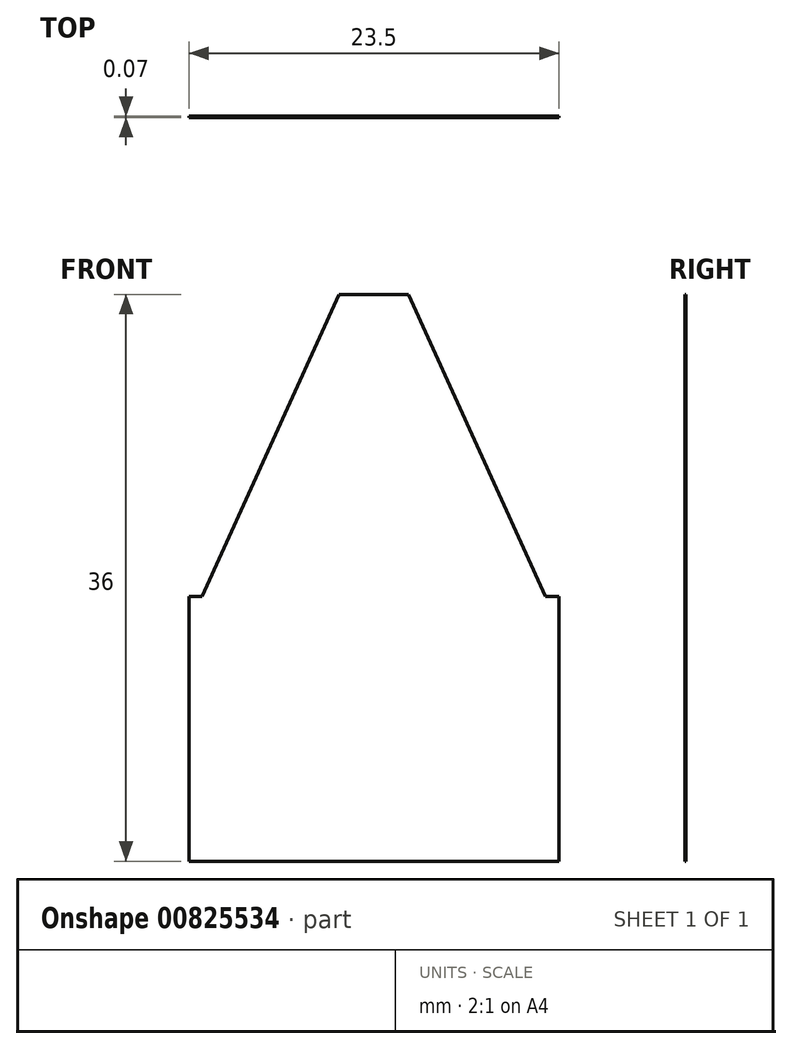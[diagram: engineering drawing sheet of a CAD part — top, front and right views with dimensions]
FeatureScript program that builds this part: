
annotation { "Feature Type Name" : "Feature", "Feature Type Description" : "" }
export const myFeature = defineFeature(function(context is Context, id is Id, definition is map)
    precondition{}
    {
        {
            var Q0;
            Q0=qCreatedBy(makeId("Front.planeOp"),FACE);
            var sketch = newSketch(context, id + "F0", { "sketchPlane" : qUnion([Q0])});
            skLineSegment(sketch, "E0.top", {"start": v(-23.9, -8.26) * mm, "end": v(-0.4, -8.26) * mm});
            skLineSegment(sketch, "E0.right", {"start": v(-0.4, 8.55) * mm, "end": v(-0.4, -8.26) * mm});
            skLineSegment(sketch, "E1", {"start": v(-23.06, 8.55) * mm, "end": v(-14.35, 27.74) * mm});
            skLineSegment(sketch, "E2", {"start": v(-9.94, 27.74) * mm, "end": v(-1.23, 8.55) * mm});
            skLineSegment(sketch, "E3", {"start": v(-23.9, 8.55) * mm, "end": v(-23.06, 8.55) * mm});
            skLineSegment(sketch, "E4", {"start": v(-1.23, 8.55) * mm, "end": v(-0.4, 8.55) * mm});
            skLineSegment(sketch, "E5.trimOffspring", {"start": v(-23.9, 6.7) * mm, "end": v(-23.9, -8.26) * mm});
            skLineSegment(sketch, "E6", {"start": v(-23.9, 6.7) * mm, "end": v(-23.9, 8.55) * mm});
            skPoint(sketch, "E7.orphan", {"position": v(-0.4, 6.7) * mm});
            skPoint(sketch, "E8.orphan", {"position": v(-0.4, 27.74) * mm});
            skPoint(sketch, "E0.left.start.orphan", {"position": v(-23.9, 27.74) * mm});
            skLineSegment(sketch, "E9", {"start": v(-14.35, 27.74) * mm, "end": v(-9.94, 27.74) * mm});
            skSolve(sketch);
        }
        {
            var Q0;
            Q0 = qSketchRegion(id + "F0", true);
            extrude(context, id + "F1", {"entities" : qUnion([Q0]), "depth" : 0.07 * mm, "offsetDistance" : 25 * mm});
        }
    });
